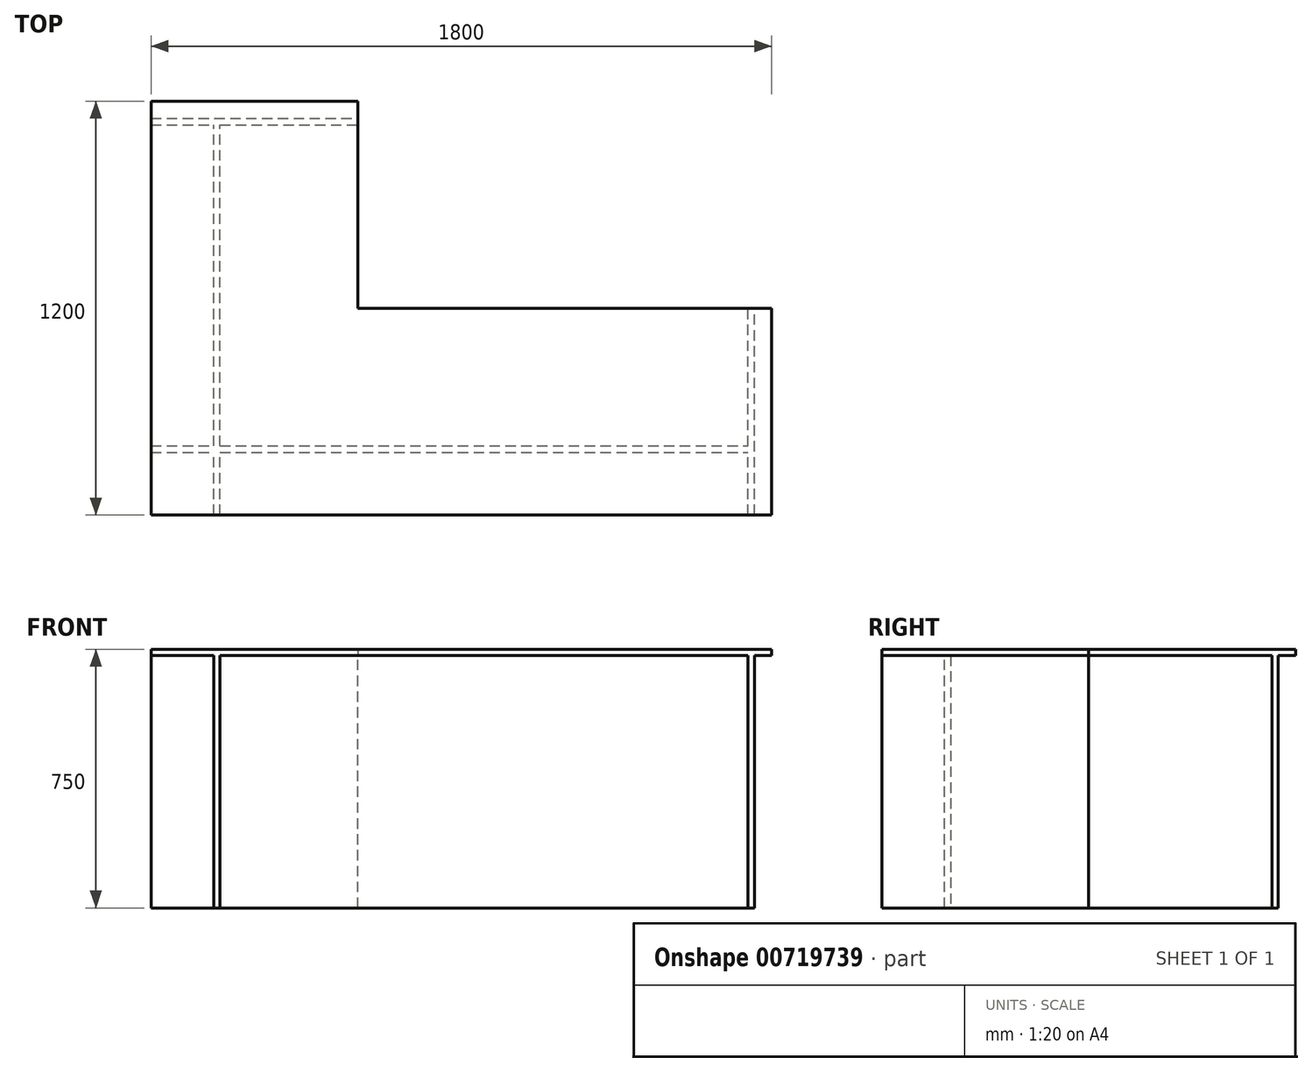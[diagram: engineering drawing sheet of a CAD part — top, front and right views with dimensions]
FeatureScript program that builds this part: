
annotation { "Feature Type Name" : "Feature", "Feature Type Description" : "" }
export const myFeature = defineFeature(function(context is Context, id is Id, definition is map)
    precondition{}
    {
        {
            var Q0;
            Q0=qCreatedBy(makeId("Top.planeOp"),FACE);
            var sketch = newSketch(context, id + "F0", { "sketchPlane" : qUnion([Q0])});
            skLineSegment(sketch, "E0.bottom", {"start": v(0, 600) * mm, "end": v(1200, 600) * mm});
            skLineSegment(sketch, "E0.top", {"start": v(0, 0) * mm, "end": v(1200, 0) * mm});
            skLineSegment(sketch, "E0.left", {"start": v(0, 600) * mm, "end": v(0, 0) * mm});
            skLineSegment(sketch, "E0.right", {"start": v(1200, 600) * mm, "end": v(1200, 0) * mm});
            skSolve(sketch);
        }
        {
            var Q0;
            Q0=makeQuery(id+"F0.imprint","IMPRINT",FACE,{"disambiguationData":[TD([[makeQuery(id+"F0.imprint","IMPRINT",EDGE,{"derivedFrom":sQuery(id+"F0.wireOp",EDGE,"E0.bottom")}),-1.0]])]});
            extrude(context, id + "F1", {"entities" : qUnion([Q0]), "depth" : 18 * mm, "offsetDistance" : 25 * mm});
        }
        {
            var Q0;
            Q0=qCreatedBy(makeId("Top.planeOp"),FACE);
            var sketch = newSketch(context, id + "F2", { "sketchPlane" : qUnion([Q0])});
            skLineSegment(sketch, "E1.bottom", {"start": v(0, 0) * mm, "end": v(-600, 0) * mm});
            skLineSegment(sketch, "E1.top", {"start": v(0, 1200) * mm, "end": v(-600, 1200) * mm});
            skLineSegment(sketch, "E1.left", {"start": v(0, 0) * mm, "end": v(0, 1200) * mm});
            skLineSegment(sketch, "E1.right", {"start": v(-600, 0) * mm, "end": v(-600, 1200) * mm});
            skSolve(sketch);
        }
        {
            var Q0;
            Q0 = qSketchRegion(id + "F2", true);
            extrude(context, id + "F3", {"entities" : qUnion([Q0]), "operationType" : NewBodyOperationType.ADD, "depth" : 18 * mm, "offsetDistance" : 25 * mm});
        }
        {
            var Q0;
            Q0=makeQuery(id+"F3.boolean.opBoolean","MERGE",FACE,{"derivedFrom":[makeQuery(id+"F1.opExtrude","CAP_FACE",FACE,{"disambiguationData":[OSD([sQuery(id+"F0.wireOp",EDGE,"E0.bottom"),sQuery(id+"F0.wireOp",EDGE,"E0.top"),sQuery(id+"F0.wireOp",EDGE,"E0.left"),sQuery(id+"F0.wireOp",EDGE,"E0.right")])],"isStart":true}),makeQuery(id+"F3.opExtrude","CAP_FACE",FACE,{"disambiguationData":[OSD([sQuery(id+"F2.wireOp",EDGE,"E1.bottom"),sQuery(id+"F2.wireOp",EDGE,"E1.top"),sQuery(id+"F2.wireOp",EDGE,"E1.left"),sQuery(id+"F2.wireOp",EDGE,"E1.right")])],"isStart":true})]});
            var sketch = newSketch(context, id + "F4", { "sketchPlane" : qUnion([Q0])});
            skLineSegment(sketch, "E2.bottom", {"start": v(1132, 0) * mm, "end": v(1150, 0) * mm});
            skLineSegment(sketch, "E2.top", {"start": v(1132, -600) * mm, "end": v(1150, -600) * mm});
            skLineSegment(sketch, "E2.left", {"start": v(1132, 0) * mm, "end": v(1132, -600) * mm});
            skLineSegment(sketch, "E2.right", {"start": v(1150, 0) * mm, "end": v(1150, -600) * mm});
            skLineSegment(sketch, "E3.bottom", {"start": v(-600, -1132) * mm, "end": v(0, -1132) * mm});
            skLineSegment(sketch, "E3.top", {"start": v(-600, -1150) * mm, "end": v(0, -1150) * mm});
            skLineSegment(sketch, "E3.left", {"start": v(-600, -1132) * mm, "end": v(-600, -1150) * mm});
            skLineSegment(sketch, "E3.right", {"start": v(0, -1132) * mm, "end": v(0, -1150) * mm});
            skSolve(sketch);
        }
        {
            var Q0;
            Q0 = qSketchRegion(id + "F4", true);
            extrude(context, id + "F5", {"entities" : qUnion([Q0]), "operationType" : NewBodyOperationType.ADD, "depth" : (750 - 18) * mm, "offsetDistance" : 25 * mm});
        }
        {
            var Q0;
            {var subQ0=sQuery(id+"F2.wireOp",EDGE,"E1.right");var subQ1=sQuery(id+"F0.wireOp",EDGE,"E0.bottom");var subQ2=sQuery(id+"F0.wireOp",EDGE,"E0.top");var subQ3=sQuery(id+"F2.wireOp",EDGE,"E1.bottom");var subQ4=sQuery(id+"F2.wireOp",EDGE,"E1.left");Q0=makeQuery(id+"F5.boolean.opBoolean","SPLIT",FACE,{"disambiguationData":[TD([makeQuery(id+"F5.opExtrude","SWEPT_FACE",FACE,{"disambiguationData":[OSD([sQuery(id+"F4.wireOp",EDGE,"E2.left")])]})])],"derivedFrom":makeQuery(id+"F3.boolean.opBoolean","MERGE",FACE,{"derivedFrom":[makeQuery(id+"F1.opExtrude","CAP_FACE",FACE,{"disambiguationData":[OSD([subQ1,subQ2,sQuery(id+"F0.wireOp",EDGE,"E0.left"),sQuery(id+"F0.wireOp",EDGE,"E0.right")])],"isStart":true}),makeQuery(id+"F3.opExtrude","CAP_FACE",FACE,{"disambiguationData":[OSD([subQ3,sQuery(id+"F2.wireOp",EDGE,"E1.top"),subQ4,subQ0])],"isStart":true})]})});}
            var sketch = newSketch(context, id + "F6", { "sketchPlane" : qUnion([Q0])});
            skLineSegment(sketch, "E4.bottom", {"start": v(-418, 0) * mm, "end": v(-400, 0) * mm});
            skLineSegment(sketch, "E4.top", {"start": v(-418, -1132) * mm, "end": v(-400, -1132) * mm});
            skLineSegment(sketch, "E4.left", {"start": v(-418, 0) * mm, "end": v(-418, -1132) * mm});
            skLineSegment(sketch, "E4.right", {"start": v(-400, 0) * mm, "end": v(-400, -1132) * mm});
            skSolve(sketch);
        }
        {
            var Q0;
            Q0 = qSketchRegion(id + "F6", true);
            extrude(context, id + "F7", {"entities" : qUnion([Q0]), "operationType" : NewBodyOperationType.ADD, "depth" : (750 - 18) * mm, "offsetDistance" : 25 * mm});
        }
        {
            var Q0;
            {var subQ0=makeQuery(id+"F5.opExtrude","SWEPT_FACE",FACE,{"disambiguationData":[OSD([sQuery(id+"F4.wireOp",EDGE,"E2.left")])]});var subQ4=sQuery(id+"F0.wireOp",EDGE,"E0.bottom");var subQ5=makeQuery(id+"F1.opExtrude","SWEPT_FACE",FACE,{"disambiguationData":[OSD([subQ4])]});var subQ7=sQuery(id+"F0.wireOp",EDGE,"E0.top");var subQ9=sQuery(id+"F2.wireOp",EDGE,"E1.bottom");var subQ11=sQuery(id+"F2.wireOp",EDGE,"E1.left");var subQ13=sQuery(id+"F2.wireOp",EDGE,"E1.right");Q0=makeQuery(id+"F7.boolean.opBoolean","SPLIT",FACE,{"disambiguationData":[TD([subQ5])],"derivedFrom":makeQuery(id+"F5.boolean.opBoolean","SPLIT",FACE,{"disambiguationData":[TD([subQ0])],"derivedFrom":makeQuery(id+"F3.boolean.opBoolean","MERGE",FACE,{"derivedFrom":[makeQuery(id+"F1.opExtrude","CAP_FACE",FACE,{"disambiguationData":[OSD([subQ4,subQ7,sQuery(id+"F0.wireOp",EDGE,"E0.left"),sQuery(id+"F0.wireOp",EDGE,"E0.right")])],"isStart":true}),makeQuery(id+"F3.opExtrude","CAP_FACE",FACE,{"disambiguationData":[OSD([subQ9,sQuery(id+"F2.wireOp",EDGE,"E1.top"),subQ11,subQ13])],"isStart":true})]})})});}
            extrude(context, id + "F8", {"entities" : qUnion([Q0]), "operationType" : NewBodyOperationType.ADD, "oppositeDirection" : true, "depth" : 18 * mm, "offsetDistance" : 25 * mm});
        }
        {
            var Q0;
            {var subQ1=sQuery(id+"F2.wireOp",EDGE,"E1.right");var subQ2=makeQuery(id+"F3.opExtrude","SWEPT_FACE",FACE,{"disambiguationData":[OSD([subQ1])]});var subQ3=sQuery(id+"F2.wireOp",EDGE,"E1.bottom");var subQ6=sQuery(id+"F0.wireOp",EDGE,"E0.top");var subQ9=sQuery(id+"F0.wireOp",EDGE,"E0.bottom");var subQ10=sQuery(id+"F2.wireOp",EDGE,"E1.left");Q0=makeQuery(id+"F7.boolean.opBoolean","SPLIT",FACE,{"disambiguationData":[TD([subQ2])],"derivedFrom":makeQuery(id+"F5.boolean.opBoolean","SPLIT",FACE,{"disambiguationData":[TD([makeQuery(id+"F5.opExtrude","SWEPT_FACE",FACE,{"disambiguationData":[OSD([sQuery(id+"F4.wireOp",EDGE,"E2.left")])]})])],"derivedFrom":makeQuery(id+"F3.boolean.opBoolean","MERGE",FACE,{"derivedFrom":[makeQuery(id+"F1.opExtrude","CAP_FACE",FACE,{"disambiguationData":[OSD([subQ9,subQ6,sQuery(id+"F0.wireOp",EDGE,"E0.left"),sQuery(id+"F0.wireOp",EDGE,"E0.right")])],"isStart":true}),makeQuery(id+"F3.opExtrude","CAP_FACE",FACE,{"disambiguationData":[OSD([subQ3,sQuery(id+"F2.wireOp",EDGE,"E1.top"),subQ10,subQ1])],"isStart":true})]})})});}
            var sketch = newSketch(context, id + "F9", { "sketchPlane" : qUnion([Q0])});
            skLineSegment(sketch, "E5.bottom", {"start": v(-600, -182) * mm, "end": v(1132, -182) * mm});
            skLineSegment(sketch, "E5.top", {"start": v(-600, -200) * mm, "end": v(1132, -200) * mm});
            skLineSegment(sketch, "E5.left", {"start": v(-600, -182) * mm, "end": v(-600, -200) * mm});
            skLineSegment(sketch, "E5.right", {"start": v(1132, -182) * mm, "end": v(1132, -200) * mm});
            skSolve(sketch);
        }
        {
            var Q0;
            Q0 = qSketchRegion(id + "F9", true);
            extrude(context, id + "F10", {"entities" : qUnion([Q0]), "operationType" : NewBodyOperationType.ADD, "depth" : (750 - 18) * mm, "offsetDistance" : 25 * mm});
        }
    });
